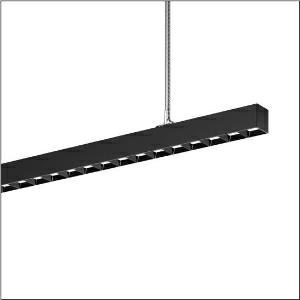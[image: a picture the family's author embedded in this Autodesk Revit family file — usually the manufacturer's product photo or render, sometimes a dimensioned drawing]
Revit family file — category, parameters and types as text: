
# Revit family: silica_r__21_51mx31dc3dbb_16a7
name_source: partatom
category: Lighting Fixtures
units: mm (PartAtom-declared; Revit-internal decimal feet)

## family parameters
Cut with Voids When Loaded = No
Host = Face
Light Source = No
Part Type = Normal
Room Calculation Point = No
Round Connector Dimension = Use Diameter
Shared = No

## types (1)
- --- (1 x LED, 18230 lm, 113.3 W, 3000K)
    Apparent Load = 113 VA
    CIE Flux Codes = 87 99 100 59 100
    Color Rendering = 80
    Color Temperature = 3000K
    Default Elevation = 1800 mm
    Description = Silica® 21, office luminaire, primary light control with darklight reflector, of PMMA, black, CAT 2 (L<= 3000cd/m²), light emission: direct/indirect distribution, primary light characteristic: symmetric, installation type: suspended mounting, LED, rated luminous flux: 18.230lm, luminous efficacy: 161lm/W, light colour: 830, colour temperature: 3000K, with terminal, 3+2-pole, max. 2.5mm², mains connection: 220..240V, AC, 50/60Hz, rated input power: 113.3W, luminaire housing, of aluminium, jet black (RAL 9005), length: 3.004mm, width: 53mm, height: 53mm, protection rating (complete): IP20, insulation class (complete): insulation class I (protective earthing), certification: CE, permissible operating ambient temperature: 0..+35°C, standard: EN 50419, packaging unit: 1 piece
    Height = 53 mm
    Lamp = 1 x LED
    Lamp Light Flux = 18230 lm
    Lamp Power = 113.3 W
    Lamp count = 1
    Length = 3004 mm
    Luminous efficacy = 161 lm/W
    Manufacturer = Siteco
    ModVariant = No
    Model = 51MX31DC3DBB
    Mounting Place = Ceiling
    Mounting Type = Pendant
    Number of Poles = 1
    OnlyDefault = Yes
    Power Factor = 1
    Product Name = Silica® 21
    Product group = office luminaire | ceiling pendant
    ProductGroupID = 902
    Protection Class = Protection class I
    Protection Degree = IP 20
    RLX_Detail_Level = 1
    RLX_Emergency_Light_Flux = 0 lm
    RLX_Emergency_Type = 0
    RLX_Emergency_Type_DB = No
    RlxData = <blob elided: 67265 chars, md5=1e3363b8>
    Socket = socket
    Standby Power = 0 W
    System Light Flux = 18230 lm
    System Power = 113 W
    Type Comments = factory setting: luminous flux: 100 % | dim-lin: 254 | 392 mA
    Type Image = l_1297774.jpg
    URL = http://relux.com
    VarID = @adj_051755
    Voltage = 0 V
    Weight = 0.00 kg
    Width = 53 mm

## geometry (parser evidence)
native form markers: Blend x4, Sweep x12
no freeform markers — native parametric forms only
